# Revit family: Estrichüberdecktes Kanalsystem EÜK_Verbindungslasche
name_source: partatom
category: Generic Models
revit_build: Autodesk Revit 2015 (Build: 20140606_1530(x64)
units: mm (PartAtom-declared; Revit-internal decimal feet)

## types (9) — shared parameters
Length = 50 mm  [stored 0.164042 ft]
Manufacturer = OBO Bettermann
Material = Steel, Galvanized
URL = http://www.obo-bettermann.com

## per-type parameters (varying)
| type | Article Type | GTIN | Height | Manufacturer Art. No. | Width |
| VL 19028E | VL 19028E | 4012195432845 | 29 mm  [stored 0.0951444 ft] | 7400960 | 191 mm  [stored 0.62664 ft] |
| VL 19038E | VL 19038E | 4012195432883 | 39 mm  [stored 0.127953 ft] | 7400962 | 191 mm  [stored 0.62664 ft] |
| VL 25028E | VL 25028E | 4012195432906 | 29 mm  [stored 0.0951444 ft] | 7400966 | 251 mm  [stored 0.823491 ft] |
| VL 35028E | VL 35028E | 4012195432968 | 49 mm  [stored 0.160761 ft] | 7400972 | 351 mm  [stored 1.15157 ft] |
| VL 25038E | VL 25038E | 4012195432944 | 39 mm  [stored 0.127953 ft] | 7400968 | 251 mm  [stored 0.823491 ft] |
| VL 35038E | VL 35038E | 4012195433002 | 39 mm  [stored 0.127953 ft] | 7400974 | 351 mm  [stored 1.15157 ft] |
| VL 19048E | VL 19048E | 4012195432890 | 49 mm  [stored 0.160761 ft] | 7400964 | 191 mm  [stored 0.62664 ft] |
| VL 25048E | VL 25048E | 4012195432951 | 49 mm  [stored 0.160761 ft] | 7400970 | 251 mm  [stored 0.823491 ft] |
| VL 35048E | VL 35049E | 4012195433019 | 49 mm  [stored 0.160761 ft] | 7400976 | 351 mm  [stored 1.15157 ft] |

note: [stored X ft] marks values corroborated as IEEE doubles in the binary element streams (Revit-internal decimal feet)

## geometry (parser evidence)
native form markers: Sweep x2
no freeform markers — native parametric forms only
